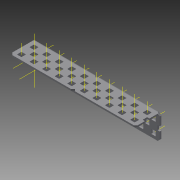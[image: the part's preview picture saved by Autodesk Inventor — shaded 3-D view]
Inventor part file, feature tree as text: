
AUTODESK INVENTOR PART (.ipt)
format: ipt  version: 2015 SP1 (Build 190203100, 203)  size: 2,011,136 bytes
history: native  units: in
note: dims shown in document units (in); Inventor stores cm internally (conversion verified against a paired STEP export)
features: other x65, pattern_linear x4, sheet_metal_op x1, extrude x1, imported_body x1, sketch x1
ambient origin geometry x8: Origin, YZ Plane, XZ Plane, XY Plane, X Axis, Y Axis, Z Axis, Center Point
bodies: Body1 (feature_tree)
feature tree (73):
  sheet_metal_op  "Fold1"
  other  "L-Channel"
  extrude  "length cut"  Depth=0.5in
  other  "top out axis"
  other  "top inner axis"
  other  "back out axis"
  other  "back inner axis"
  pattern_linear  "top outer axes"  Count1=2 Spacing1=0.5in
  pattern_linear  "top inner axes"  Spacing1=0.5in  [1 undecoded]
  pattern_linear  "back outer axes"  Count1=2 Spacing1=0.5in
  pattern_linear  "back inner axes"  Spacing1=0.5in  [1 undecoded]
  other  "right plane"
  imported_body  "Base1"
  sketch  "Sketch1"  dims[d1=0.0in d4=0.5in d5=0.7874in d7=0.5in d10=0.5in d13=0.5in d14=0.7874in d16=0.5in d19=0.5in d20=-5.0in d21=0.0in d22=0.0in d23=0.0in d24=0.0in d25=0.0in d26=0.0in]
  other  "Work Point1"
  other  "Work Point2"
  other  "Work Point3"
  other  "Work Point4"
  other  "Work Axis5"
  other  "Work Axis6"
  other  "Work Axis7"
  other  "Work Axis8"
  other  "Work Axis11"
  other  "Work Axis12"
  other  "Work Axis13"
  other  "Work Axis14"
  other  "Work Axis15"
  other  "Work Axis18"
  other  "Work Axis19"
  other  "Work Axis20"
  other  "Work Axis23"
  other  "Work Axis24"
  other  "Work Axis25"
  other  "Work Axis26"
  other  "Work Axis29"
  other  "Work Axis30"
  other  "Work Axis31"
  other  "Work Axis32"
  other  "Work Axis33"
  other  "Work Axis36"
  other  "Work Axis37"
  other  "Work Axis38"
  other  "Work Axis41"
  other  "Work Axis42"
  other  "Work Axis43"
  other  "Work Axis44"
  other  "Work Axis45"
  other  "Work Axis61"
  other  "Work Axis62"
  other  "Work Axis63"
  other  "Work Axis64"
  other  "Work Axis65"
  other  "Work Axis81"
  other  "Work Axis82"
  other  "Work Axis83"
  other  "Work Axis84"
  other  "Work Axis85"
  other  "Work Axis101"
  other  "Work Axis102"
  other  "Work Axis103"
  other  "Work Axis104"
  other  "Work Axis105"
  other  "Work Axis121"
  other  "Work Axis122"
  other  "Work Axis123"
  other  "Work Axis124"
  other  "Work Axis125"
  other  "Work Axis141"
  other  "Work Axis142"
  other  "Work Axis143"
  other  "Work Axis144"
  other  "Work Axis145"
  other  "left plane"
note: 2 required parameter values undecoded (feature->parameter linkage not recoverable at this tier; creation-order binding heuristic only, values carry confidence <= 0.55)
